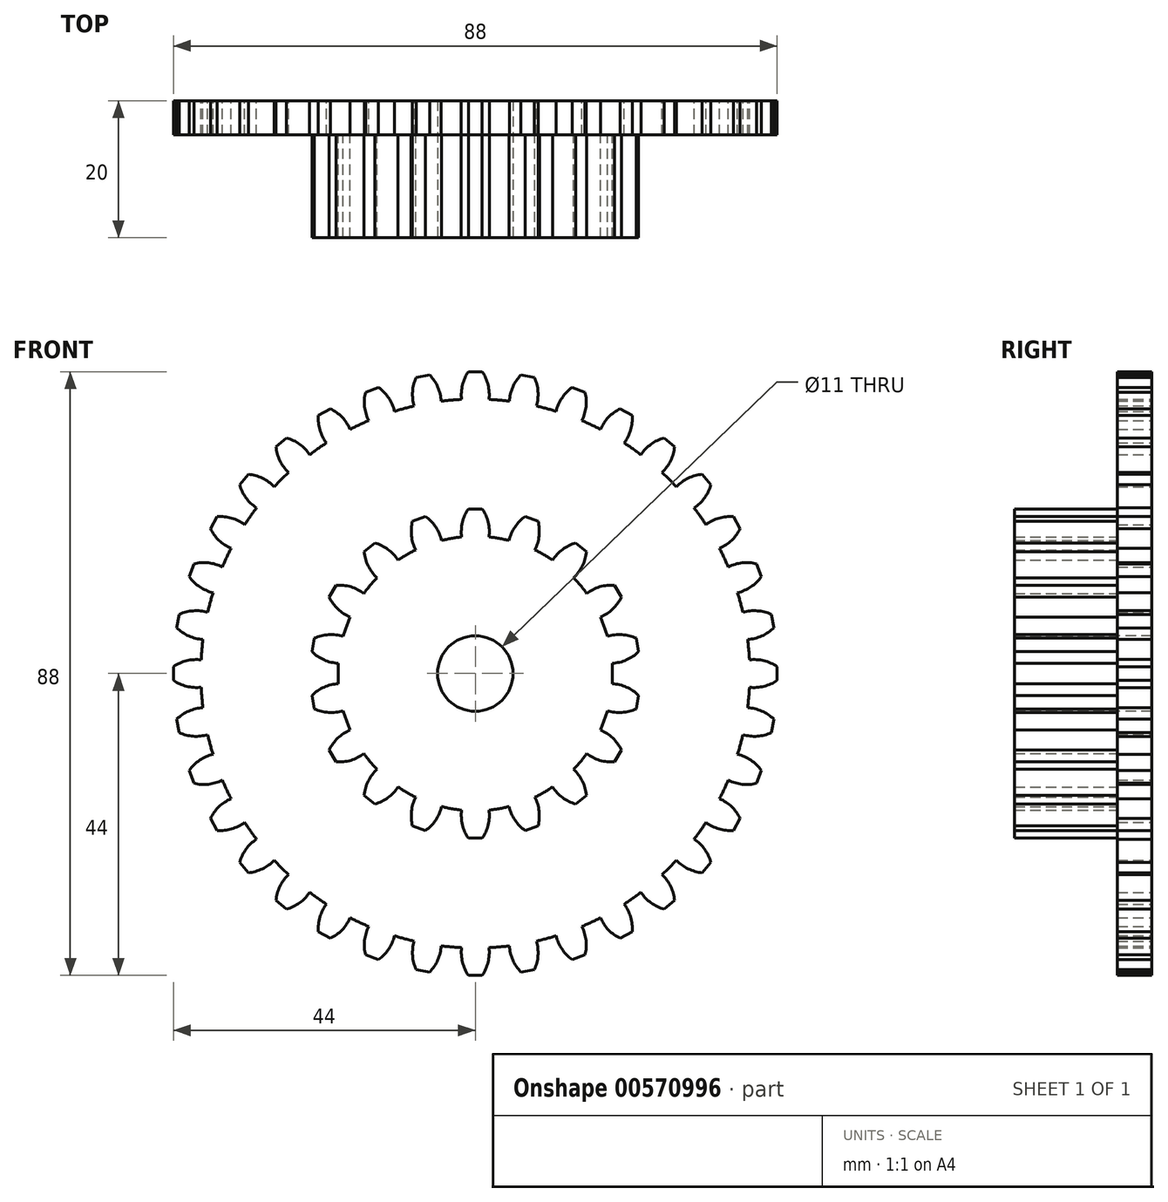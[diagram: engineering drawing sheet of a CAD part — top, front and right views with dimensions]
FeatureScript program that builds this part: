
annotation { "Feature Type Name" : "Feature", "Feature Type Description" : "" }
export const myFeature = defineFeature(function(context is Context, id is Id, definition is map)
    precondition{}
    {
        {
            var Q0;
            Q0=qCreatedBy(makeId("Front.planeOp"),FACE);
            var sketch = newSketch(context, id + "F0", { "sketchPlane" : qUnion([Q0])});
            skCircle(sketch, "E0", {"center": v(0, 0) * mm, "radius": 40 * mm});
            skLineSegment(sketch, "E1", {"start": v(-1, 44) * mm, "end": v(1, 44) * mm});
            skArc(sketch, "E2", {"start": v(2, 39.95) * mm, "mid": v(1.86, 42.06) * mm, "end": v(1, 44) * mm});
            skArc(sketch, "E3", {"start": v(-1, 44) * mm, "mid": v(-1.86, 42.06) * mm, "end": v(-2, 39.95) * mm});
            skSolve(sketch);
        }
        {
            var Q0;
            {var subQ0=sQuery(id+"F0.wireOp",EDGE,"E0");var subQ1=makeQuery(id+"F0.imprint","INTERSECT",VERTEX,{"derivedFrom":[subQ0,sQuery(id+"F0.wireOp",EDGE,"E2")]});Q0=makeQuery(id+"F0.imprint","IMPRINT",FACE,{"disambiguationData":[TD([[makeQuery(id+"F0.imprint","IMPRINT",EDGE,{"disambiguationData":[TD([[subQ1,-1.0]])],"derivedFrom":subQ0}),1.0]])]});}
            var Q1;
            Q1=makeQuery(id+"F0.imprint","IMPRINT",FACE,{"disambiguationData":[TD([[makeQuery(id+"F0.imprint","IMPRINT",EDGE,{"derivedFrom":sQuery(id+"F0.wireOp",EDGE,"E1")}),-1.0]])]});
            extrude(context, id + "F1", {"entities" : qUnion([Q0, Q1]), "depth" : 5 * mm, "offsetDistance" : 25 * mm, "symmetric" : true});
        }
        {
            var Q0;
            {var subQ0=makeQuery(id+"F1.opExtrude","CAP_FACE",FACE,{"disambiguationData":[OSD([sQuery(id+"F0.wireOp",EDGE,"E0"),sQuery(id+"F0.wireOp",EDGE,"E1"),sQuery(id+"F0.wireOp",EDGE,"E2"),sQuery(id+"F0.wireOp",EDGE,"E3")])],"isStart":false});Q0=makeQuery(id+"F3.boolean.opBoolean","MERGE",FACE,{"derivedFrom":[subQ0,makeQuery(id+"F3.opPattern","COPY",FACE,{"derivedFrom":subQ0,"instanceName":"1"}),makeQuery(id+"F3.opPattern","COPY",FACE,{"derivedFrom":subQ0,"instanceName":"2"}),makeQuery(id+"F3.opPattern","COPY",FACE,{"derivedFrom":subQ0,"instanceName":"3"}),makeQuery(id+"F3.opPattern","COPY",FACE,{"derivedFrom":subQ0,"instanceName":"4"}),makeQuery(id+"F3.opPattern","COPY",FACE,{"derivedFrom":subQ0,"instanceName":"5"}),makeQuery(id+"F3.opPattern","COPY",FACE,{"derivedFrom":subQ0,"instanceName":"6"}),makeQuery(id+"F3.opPattern","COPY",FACE,{"derivedFrom":subQ0,"instanceName":"7"}),makeQuery(id+"F3.opPattern","COPY",FACE,{"derivedFrom":subQ0,"instanceName":"8"}),makeQuery(id+"F3.opPattern","COPY",FACE,{"derivedFrom":subQ0,"instanceName":"9"}),makeQuery(id+"F3.opPattern","COPY",FACE,{"derivedFrom":subQ0,"instanceName":"10"}),makeQuery(id+"F3.opPattern","COPY",FACE,{"derivedFrom":subQ0,"instanceName":"11"}),makeQuery(id+"F3.opPattern","COPY",FACE,{"derivedFrom":subQ0,"instanceName":"12"}),makeQuery(id+"F3.opPattern","COPY",FACE,{"derivedFrom":subQ0,"instanceName":"13"}),makeQuery(id+"F3.opPattern","COPY",FACE,{"derivedFrom":subQ0,"instanceName":"14"}),makeQuery(id+"F3.opPattern","COPY",FACE,{"derivedFrom":subQ0,"instanceName":"15"}),makeQuery(id+"F3.opPattern","COPY",FACE,{"derivedFrom":subQ0,"instanceName":"16"}),makeQuery(id+"F3.opPattern","COPY",FACE,{"derivedFrom":subQ0,"instanceName":"17"}),makeQuery(id+"F3.opPattern","COPY",FACE,{"derivedFrom":subQ0,"instanceName":"18"}),makeQuery(id+"F3.opPattern","COPY",FACE,{"derivedFrom":subQ0,"instanceName":"19"}),makeQuery(id+"F3.opPattern","COPY",FACE,{"derivedFrom":subQ0,"instanceName":"20"}),makeQuery(id+"F3.opPattern","COPY",FACE,{"derivedFrom":subQ0,"instanceName":"21"}),makeQuery(id+"F3.opPattern","COPY",FACE,{"derivedFrom":subQ0,"instanceName":"22"}),makeQuery(id+"F3.opPattern","COPY",FACE,{"derivedFrom":subQ0,"instanceName":"23"}),makeQuery(id+"F3.opPattern","COPY",FACE,{"derivedFrom":subQ0,"instanceName":"24"}),makeQuery(id+"F3.opPattern","COPY",FACE,{"derivedFrom":subQ0,"instanceName":"25"}),makeQuery(id+"F3.opPattern","COPY",FACE,{"derivedFrom":subQ0,"instanceName":"26"}),makeQuery(id+"F3.opPattern","COPY",FACE,{"derivedFrom":subQ0,"instanceName":"27"}),makeQuery(id+"F3.opPattern","COPY",FACE,{"derivedFrom":subQ0,"instanceName":"28"}),makeQuery(id+"F3.opPattern","COPY",FACE,{"derivedFrom":subQ0,"instanceName":"29"}),makeQuery(id+"F3.opPattern","COPY",FACE,{"derivedFrom":subQ0,"instanceName":"30"}),makeQuery(id+"F3.opPattern","COPY",FACE,{"derivedFrom":subQ0,"instanceName":"31"}),makeQuery(id+"F3.opPattern","COPY",FACE,{"derivedFrom":subQ0,"instanceName":"32"}),makeQuery(id+"F3.opPattern","COPY",FACE,{"derivedFrom":subQ0,"instanceName":"33"}),makeQuery(id+"F3.opPattern","COPY",FACE,{"derivedFrom":subQ0,"instanceName":"34"})]});}
            var sketch = newSketch(context, id + "F2", { "sketchPlane" : qUnion([Q0])});
            skCircle(sketch, "E4", {"center": v(0, 0) * mm, "radius": 5.5 * mm});
            skSolve(sketch);
        }
        {
            var Q0;
            Q0=makeQuery(id+"F1.opExtrude","SWEPT_BODY",BODY,{"disambiguationData":[OSD([sQuery(id+"F0.wireOp",EDGE,"E0"),sQuery(id+"F0.wireOp",EDGE,"E1"),sQuery(id+"F0.wireOp",EDGE,"E2"),sQuery(id+"F0.wireOp",EDGE,"E3")])]});
            var Q1;
            Q1=makeQuery(id+"F1.opExtrude","SWEPT_FACE",FACE,{"disambiguationData":[OSD([sQuery(id+"F0.wireOp",EDGE,"E0")])]});
            circularPattern(context, id + "F3", {"operationType" : NewBodyOperationType.ADD, "entities" : qUnion([Q0]), "axis" : qUnion([Q1]), "angle" : 360 * degree, "instanceCount" : 36, "equalSpace" : true});
        }
        {
            var Q0;
            Q0=makeQuery(id+"F2.imprint","IMPRINT",FACE,{"disambiguationData":[TD([[makeQuery(id+"F2.imprint","IMPRINT",EDGE,{"derivedFrom":sQuery(id+"F2.wireOp",EDGE,"E4")}),1.0]])]});
            extrude(context, id + "F4", {"entities" : qUnion([Q0]), "operationType" : NewBodyOperationType.REMOVE, "oppositeDirection" : true, "depth" : 25 * mm, "offsetDistance" : 25 * mm});
        }
        {
            var Q0;
            {var subQ0=makeQuery(id+"F1.opExtrude","CAP_FACE",FACE,{"disambiguationData":[OSD([sQuery(id+"F0.wireOp",EDGE,"E0"),sQuery(id+"F0.wireOp",EDGE,"E1"),sQuery(id+"F0.wireOp",EDGE,"E2"),sQuery(id+"F0.wireOp",EDGE,"E3")])],"isStart":false});Q0=makeQuery(id+"F3.boolean.opBoolean","MERGE",FACE,{"derivedFrom":[subQ0,makeQuery(id+"F3.opPattern","COPY",FACE,{"derivedFrom":subQ0,"instanceName":"1"}),makeQuery(id+"F3.opPattern","COPY",FACE,{"derivedFrom":subQ0,"instanceName":"2"}),makeQuery(id+"F3.opPattern","COPY",FACE,{"derivedFrom":subQ0,"instanceName":"3"}),makeQuery(id+"F3.opPattern","COPY",FACE,{"derivedFrom":subQ0,"instanceName":"4"}),makeQuery(id+"F3.opPattern","COPY",FACE,{"derivedFrom":subQ0,"instanceName":"5"}),makeQuery(id+"F3.opPattern","COPY",FACE,{"derivedFrom":subQ0,"instanceName":"6"}),makeQuery(id+"F3.opPattern","COPY",FACE,{"derivedFrom":subQ0,"instanceName":"7"}),makeQuery(id+"F3.opPattern","COPY",FACE,{"derivedFrom":subQ0,"instanceName":"8"}),makeQuery(id+"F3.opPattern","COPY",FACE,{"derivedFrom":subQ0,"instanceName":"9"}),makeQuery(id+"F3.opPattern","COPY",FACE,{"derivedFrom":subQ0,"instanceName":"10"}),makeQuery(id+"F3.opPattern","COPY",FACE,{"derivedFrom":subQ0,"instanceName":"11"}),makeQuery(id+"F3.opPattern","COPY",FACE,{"derivedFrom":subQ0,"instanceName":"12"}),makeQuery(id+"F3.opPattern","COPY",FACE,{"derivedFrom":subQ0,"instanceName":"13"}),makeQuery(id+"F3.opPattern","COPY",FACE,{"derivedFrom":subQ0,"instanceName":"14"}),makeQuery(id+"F3.opPattern","COPY",FACE,{"derivedFrom":subQ0,"instanceName":"15"}),makeQuery(id+"F3.opPattern","COPY",FACE,{"derivedFrom":subQ0,"instanceName":"16"}),makeQuery(id+"F3.opPattern","COPY",FACE,{"derivedFrom":subQ0,"instanceName":"17"}),makeQuery(id+"F3.opPattern","COPY",FACE,{"derivedFrom":subQ0,"instanceName":"18"}),makeQuery(id+"F3.opPattern","COPY",FACE,{"derivedFrom":subQ0,"instanceName":"19"}),makeQuery(id+"F3.opPattern","COPY",FACE,{"derivedFrom":subQ0,"instanceName":"20"}),makeQuery(id+"F3.opPattern","COPY",FACE,{"derivedFrom":subQ0,"instanceName":"21"}),makeQuery(id+"F3.opPattern","COPY",FACE,{"derivedFrom":subQ0,"instanceName":"22"}),makeQuery(id+"F3.opPattern","COPY",FACE,{"derivedFrom":subQ0,"instanceName":"23"}),makeQuery(id+"F3.opPattern","COPY",FACE,{"derivedFrom":subQ0,"instanceName":"24"}),makeQuery(id+"F3.opPattern","COPY",FACE,{"derivedFrom":subQ0,"instanceName":"25"}),makeQuery(id+"F3.opPattern","COPY",FACE,{"derivedFrom":subQ0,"instanceName":"26"}),makeQuery(id+"F3.opPattern","COPY",FACE,{"derivedFrom":subQ0,"instanceName":"27"}),makeQuery(id+"F3.opPattern","COPY",FACE,{"derivedFrom":subQ0,"instanceName":"28"}),makeQuery(id+"F3.opPattern","COPY",FACE,{"derivedFrom":subQ0,"instanceName":"29"}),makeQuery(id+"F3.opPattern","COPY",FACE,{"derivedFrom":subQ0,"instanceName":"30"}),makeQuery(id+"F3.opPattern","COPY",FACE,{"derivedFrom":subQ0,"instanceName":"31"}),makeQuery(id+"F3.opPattern","COPY",FACE,{"derivedFrom":subQ0,"instanceName":"32"}),makeQuery(id+"F3.opPattern","COPY",FACE,{"derivedFrom":subQ0,"instanceName":"33"}),makeQuery(id+"F3.opPattern","COPY",FACE,{"derivedFrom":subQ0,"instanceName":"34"})]});}
            var sketch = newSketch(context, id + "F5", { "sketchPlane" : qUnion([Q0])});
            skCircle(sketch, "E5", {"center": v(0, 0) * mm, "radius": 20 * mm});
            skCircle(sketch, "E6", {"center": v(0, 0) * mm, "radius": 5.5 * mm});
            skLineSegment(sketch, "E7", {"start": v(-1, 24) * mm, "end": v(1, 24) * mm});
            skArc(sketch, "E8", {"start": v(2, 19.9) * mm, "mid": v(1.87, 22.04) * mm, "end": v(1, 24) * mm});
            skArc(sketch, "E9", {"start": v(-1, 24) * mm, "mid": v(-1.87, 22.04) * mm, "end": v(-2, 19.9) * mm});
            skSolve(sketch);
        }
        {
            var Q0;
            Q0=makeQuery(id+"F5.imprint","IMPRINT",FACE,{"disambiguationData":[TD([[makeQuery(id+"F5.imprint","IMPRINT",EDGE,{"derivedFrom":sQuery(id+"F5.wireOp",EDGE,"E7")}),-1.0]])]});
            var Q1;
            Q1=makeQuery(id+"F5.imprint","IMPRINT",FACE,{"disambiguationData":[TD([[makeQuery(id+"F5.imprint","IMPRINT",EDGE,{"derivedFrom":sQuery(id+"F5.wireOp",EDGE,"E6")}),-1.0]])]});
            extrude(context, id + "F6", {"entities" : qUnion([Q0, Q1]), "depth" : 15 * mm, "offsetDistance" : 25 * mm});
        }
        {
            var Q0;
            Q0=makeQuery(id+"F6.opExtrude","SWEPT_BODY",BODY,{"disambiguationData":[OSD([sQuery(id+"F5.wireOp",EDGE,"E5"),sQuery(id+"F5.wireOp",EDGE,"E6"),sQuery(id+"F5.wireOp",EDGE,"E7"),sQuery(id+"F5.wireOp",EDGE,"E8"),sQuery(id+"F5.wireOp",EDGE,"E9")])]});
            var Q1;
            Q1=makeQuery(id+"F6.opExtrude","SWEPT_FACE",FACE,{"disambiguationData":[OSD([sQuery(id+"F5.wireOp",EDGE,"E5")])]});
            circularPattern(context, id + "F7", {"operationType" : NewBodyOperationType.ADD, "entities" : qUnion([Q0]), "axis" : qUnion([Q1]), "angle" : 360 * degree, "instanceCount" : 18, "equalSpace" : true});
        }
    });
